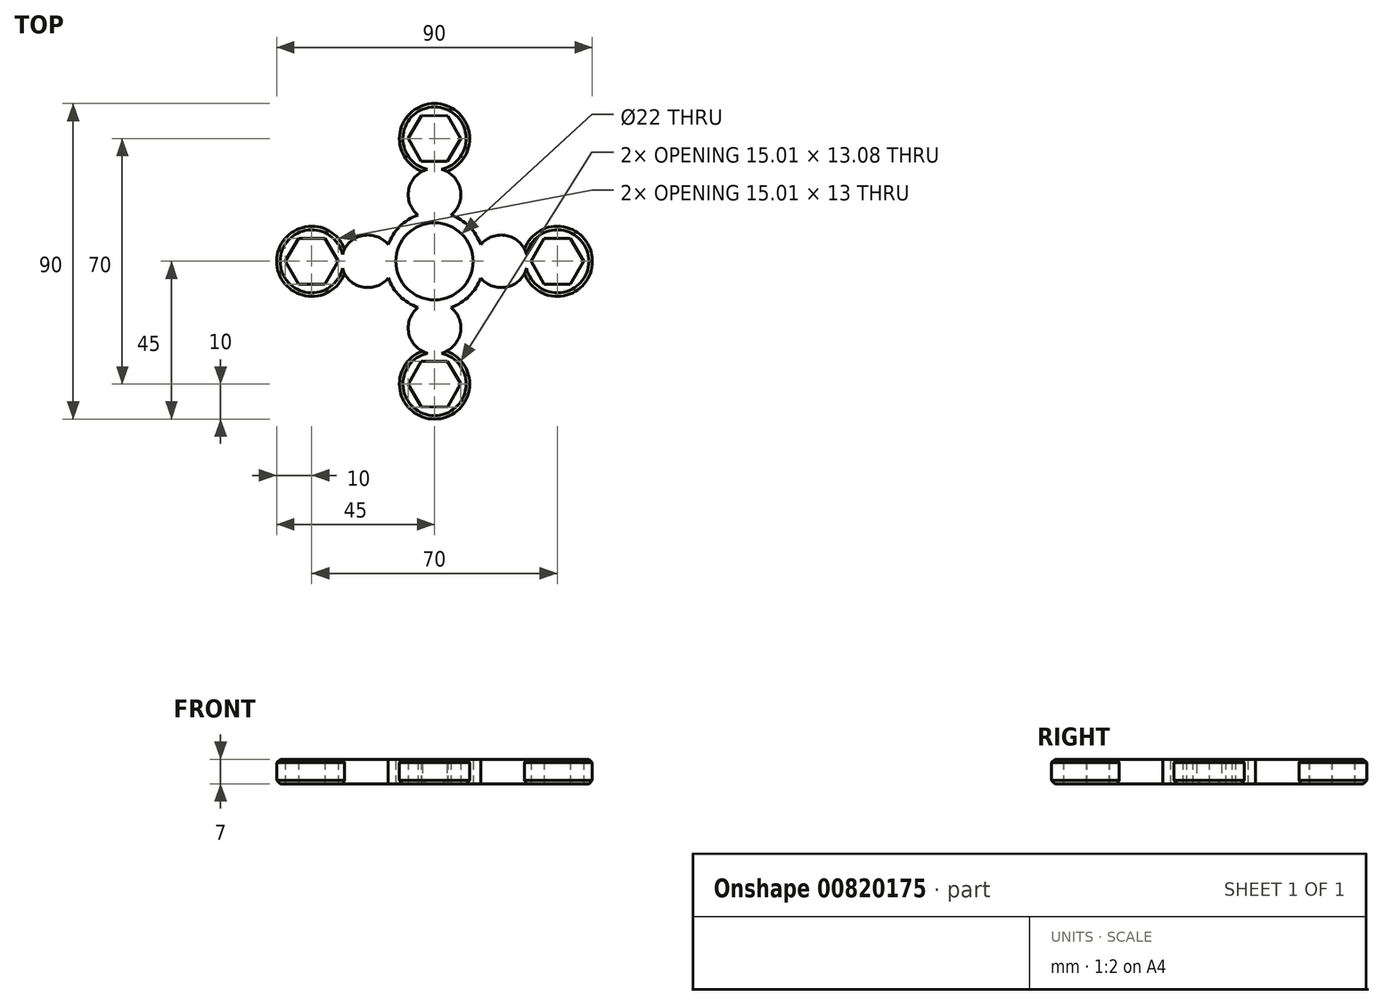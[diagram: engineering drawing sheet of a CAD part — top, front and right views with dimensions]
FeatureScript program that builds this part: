
annotation { "Feature Type Name" : "Feature", "Feature Type Description" : "" }
export const myFeature = defineFeature(function(context is Context, id is Id, definition is map)
    precondition{}
    {
        {
            var Q0;
            Q0=qCreatedBy(makeId("Top.planeOp"),FACE);
            var sketch = newSketch(context, id + "F0", { "sketchPlane" : qUnion([Q0])});
            skCircle(sketch, "E0", {"center": v(0, 0) * mm, "radius": 11 * mm});
            skCircle(sketch, "E1", {"center": v(0, 0) * mm, "radius": 14 * mm});
            skCircle(sketch, "E2", {"center": v(0, 19) * mm, "radius": 7.5 * mm});
            skCircle(sketch, "E3.MirrorC", {"center": v(0, -19) * mm, "radius": 7.5 * mm});
            skCircle(sketch, "E4", {"center": v(-19, 0) * mm, "radius": 7.5 * mm});
            skCircle(sketch, "E5.MirrorC", {"center": v(19, 0) * mm, "radius": 7.5 * mm});
            skCircle(sketch, "E6", {"center": v(-35, 0) * mm, "radius": 10 * mm});
            skCircle(sketch, "E7.MirrorC", {"center": v(35, 0) * mm, "radius": 10 * mm});
            skCircle(sketch, "E8", {"center": v(0, 35) * mm, "radius": 10 * mm});
            skCircle(sketch, "E9.MirrorC", {"center": v(0, -35) * mm, "radius": 10 * mm});
            skCircle(sketch, "E10.cCircle", {"center": v(0, 35) * mm, "radius": 6.5 * mm, "construction": true});
            skLineSegment(sketch, "E10.0", {"start": v(3.82, 41.46) * mm, "end": v(7.5, 34.92) * mm});
            skLineSegment(sketch, "E10.1", {"start": v(7.5, 34.92) * mm, "end": v(3.68, 28.46) * mm});
            skLineSegment(sketch, "E10.2", {"start": v(3.68, 28.46) * mm, "end": v(-3.82, 28.54) * mm});
            skLineSegment(sketch, "E10.3", {"start": v(-3.82, 28.54) * mm, "end": v(-7.5, 35.08) * mm});
            skLineSegment(sketch, "E10.4", {"start": v(-7.5, 35.08) * mm, "end": v(-3.68, 41.54) * mm});
            skLineSegment(sketch, "E10.5", {"start": v(-3.68, 41.54) * mm, "end": v(3.82, 41.46) * mm});
            skPoint(sketch, "E10.0.midPoint", {"position": v(5.66, 38.2) * mm});
            skLineSegment(sketch, "E11.MirrorCS", {"start": v(-3.68, -41.54) * mm, "end": v(3.82, -41.46) * mm});
            skCircle(sketch, "E12.MirrorC", {"center": v(0, -35) * mm, "radius": 6.5 * mm, "construction": true});
            skLineSegment(sketch, "E13.MirrorCS", {"start": v(3.82, -41.46) * mm, "end": v(7.5, -34.92) * mm});
            skLineSegment(sketch, "E14.MirrorCS", {"start": v(7.5, -34.92) * mm, "end": v(3.68, -28.46) * mm});
            skLineSegment(sketch, "E15.MirrorCS", {"start": v(3.68, -28.46) * mm, "end": v(-3.82, -28.54) * mm});
            skLineSegment(sketch, "E16.MirrorCS", {"start": v(-3.82, -28.54) * mm, "end": v(-7.5, -35.08) * mm});
            skLineSegment(sketch, "E17.MirrorCS", {"start": v(-7.5, -35.08) * mm, "end": v(-3.68, -41.54) * mm});
            skCircle(sketch, "E18.cCircle", {"center": v(35, 0) * mm, "radius": 6.5 * mm, "construction": true});
            skLineSegment(sketch, "E18.0", {"start": v(38.75, 6.5) * mm, "end": v(42.5, 0) * mm});
            skLineSegment(sketch, "E18.1", {"start": v(42.5, 0) * mm, "end": v(38.76, -6.5) * mm});
            skLineSegment(sketch, "E18.2", {"start": v(38.76, -6.5) * mm, "end": v(31.25, -6.5) * mm});
            skLineSegment(sketch, "E18.3", {"start": v(31.25, -6.5) * mm, "end": v(27.5, 0) * mm});
            skLineSegment(sketch, "E18.4", {"start": v(27.5, 0) * mm, "end": v(31.24, 6.5) * mm});
            skLineSegment(sketch, "E18.5", {"start": v(31.24, 6.5) * mm, "end": v(38.75, 6.5) * mm});
            skPoint(sketch, "E18.0.midPoint", {"position": v(40.63, 3.25) * mm});
            skLineSegment(sketch, "E19.MirrorCS", {"start": v(-31.24, 6.5) * mm, "end": v(-38.75, 6.5) * mm});
            skLineSegment(sketch, "E20.MirrorCS", {"start": v(-27.5, 0) * mm, "end": v(-31.24, 6.5) * mm});
            skLineSegment(sketch, "E21.MirrorCS", {"start": v(-31.25, -6.5) * mm, "end": v(-27.5, 0) * mm});
            skLineSegment(sketch, "E22.MirrorCS", {"start": v(-38.76, -6.5) * mm, "end": v(-31.25, -6.5) * mm});
            skLineSegment(sketch, "E23.MirrorCS", {"start": v(-42.5, 0) * mm, "end": v(-38.76, -6.5) * mm});
            skCircle(sketch, "E24.MirrorC", {"center": v(-35, 0) * mm, "radius": 6.5 * mm, "construction": true});
            skLineSegment(sketch, "E25.MirrorCS", {"start": v(-38.75, 6.5) * mm, "end": v(-42.5, 0) * mm});
            skSolve(sketch);
        }
        {
            var Q0;
            Q0 = qSketchRegion(id + "F0", true);
            extrude(context, id + "F1", {"entities" : qUnion([Q0]), "depth" : 7 * mm, "offsetDistance" : 25 * mm});
        }
        {
            var Q0;
            Q0=makeQuery(id+"F1.opExtrude","CAP_EDGE",EDGE,{"disambiguationData":[OSD([sQuery(id+"F0.wireOp",EDGE,"E6")])],"isStart":false});
            var Q1;
            Q1=makeQuery(id+"F1.opExtrude","CAP_EDGE",EDGE,{"disambiguationData":[OSD([sQuery(id+"F0.wireOp",EDGE,"E8")])],"isStart":false});
            var Q2;
            Q2=makeQuery(id+"F1.opExtrude","CAP_EDGE",EDGE,{"disambiguationData":[OSD([sQuery(id+"F0.wireOp",EDGE,"E9.MirrorC")])],"isStart":false});
            var Q3;
            Q3=makeQuery(id+"F1.opExtrude","CAP_EDGE",EDGE,{"disambiguationData":[OSD([sQuery(id+"F0.wireOp",EDGE,"E7.MirrorC")])],"isStart":false});
            chamfer(context, id + "F2", {"entities" : qUnion([Q0, Q1, Q2, Q3]), "width" : 1 * mm, "tangentPropagation" : true});
        }
        {
            var Q0;
            Q0=makeQuery(id+"F1.opExtrude","CAP_EDGE",EDGE,{"disambiguationData":[OSD([sQuery(id+"F0.wireOp",EDGE,"E6")])],"isStart":true});
            var Q1;
            Q1=makeQuery(id+"F1.opExtrude","CAP_EDGE",EDGE,{"disambiguationData":[OSD([sQuery(id+"F0.wireOp",EDGE,"E9.MirrorC")])],"isStart":true});
            var Q2;
            Q2=makeQuery(id+"F1.opExtrude","CAP_EDGE",EDGE,{"disambiguationData":[OSD([sQuery(id+"F0.wireOp",EDGE,"E7.MirrorC")])],"isStart":true});
            var Q3;
            Q3=makeQuery(id+"F1.opExtrude","CAP_EDGE",EDGE,{"disambiguationData":[OSD([sQuery(id+"F0.wireOp",EDGE,"E8")])],"isStart":true});
            chamfer(context, id + "F3", {"entities" : qUnion([Q0, Q1, Q2, Q3]), "width" : 1 * mm, "tangentPropagation" : true});
        }
    });
